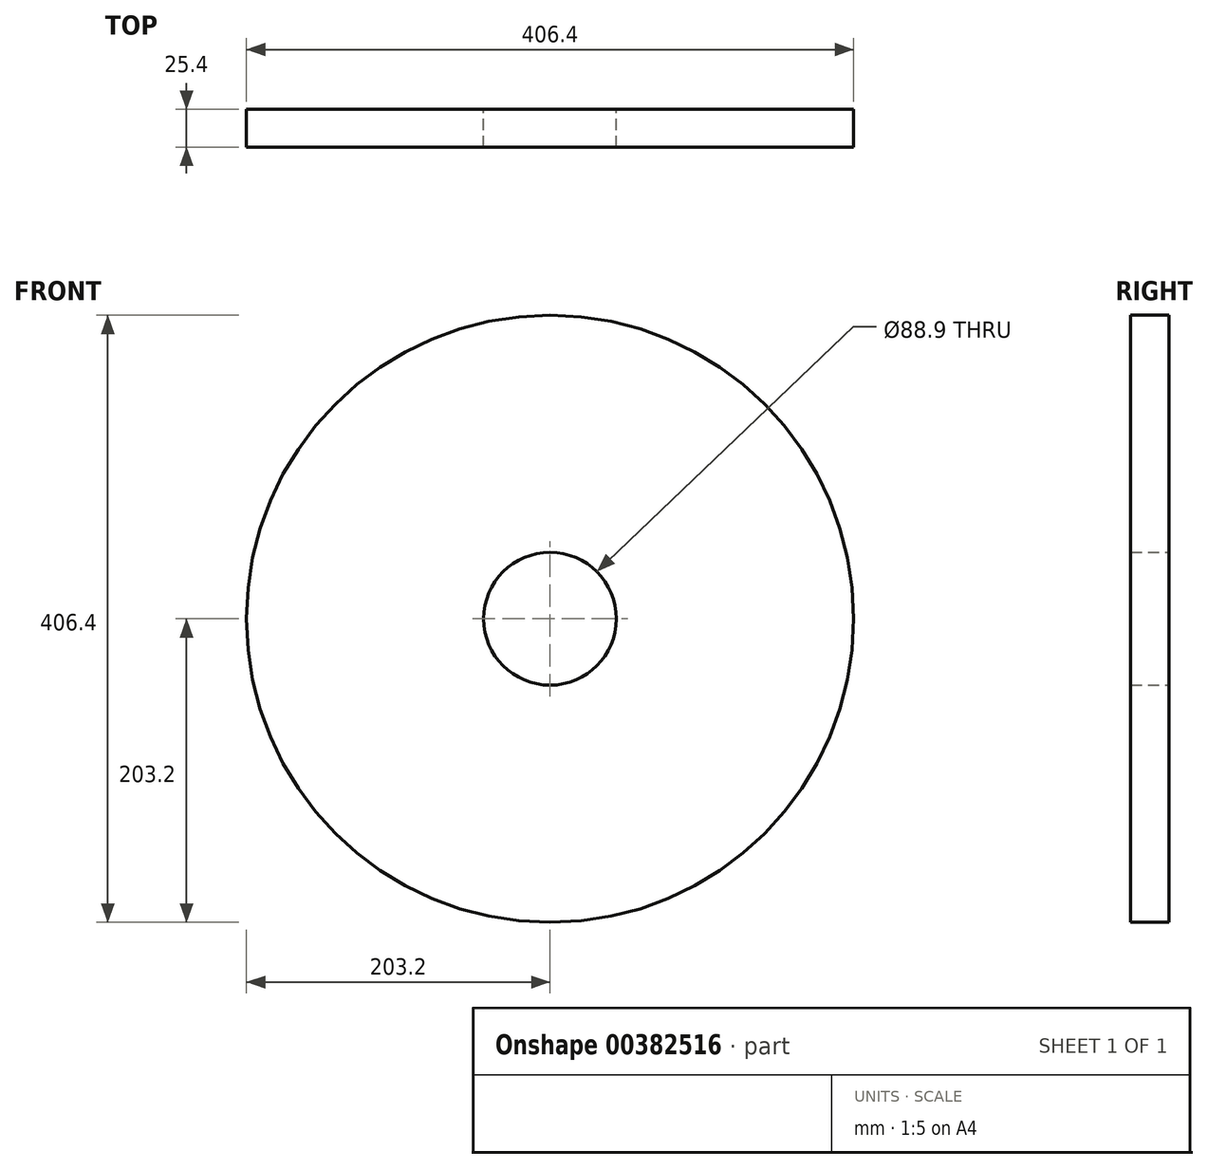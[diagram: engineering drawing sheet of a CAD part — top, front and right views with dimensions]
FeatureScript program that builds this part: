
annotation { "Feature Type Name" : "Feature", "Feature Type Description" : "" }
export const myFeature = defineFeature(function(context is Context, id is Id, definition is map)
    precondition{}
    {
        {
            var Q0;
            Q0=qCreatedBy(makeId("Front.planeOp"),FACE);
            var sketch = newSketch(context, id + "F0", { "sketchPlane" : qUnion([Q0])});
            skCircle(sketch, "E0.0", {"center": v(0, 0) * mm, "radius": 203.2 * mm});
            skCircle(sketch, "E1.0", {"center": v(0, 0) * mm, "radius": 44.45 * mm});
            skSolve(sketch);
        }
        {
            var Q0;
            Q0 = qSketchRegion(id + "F0", true);
            extrude(context, id + "F1", {"entities" : qUnion([Q0]), "depth" : 25.4 * mm});
        }
    });
